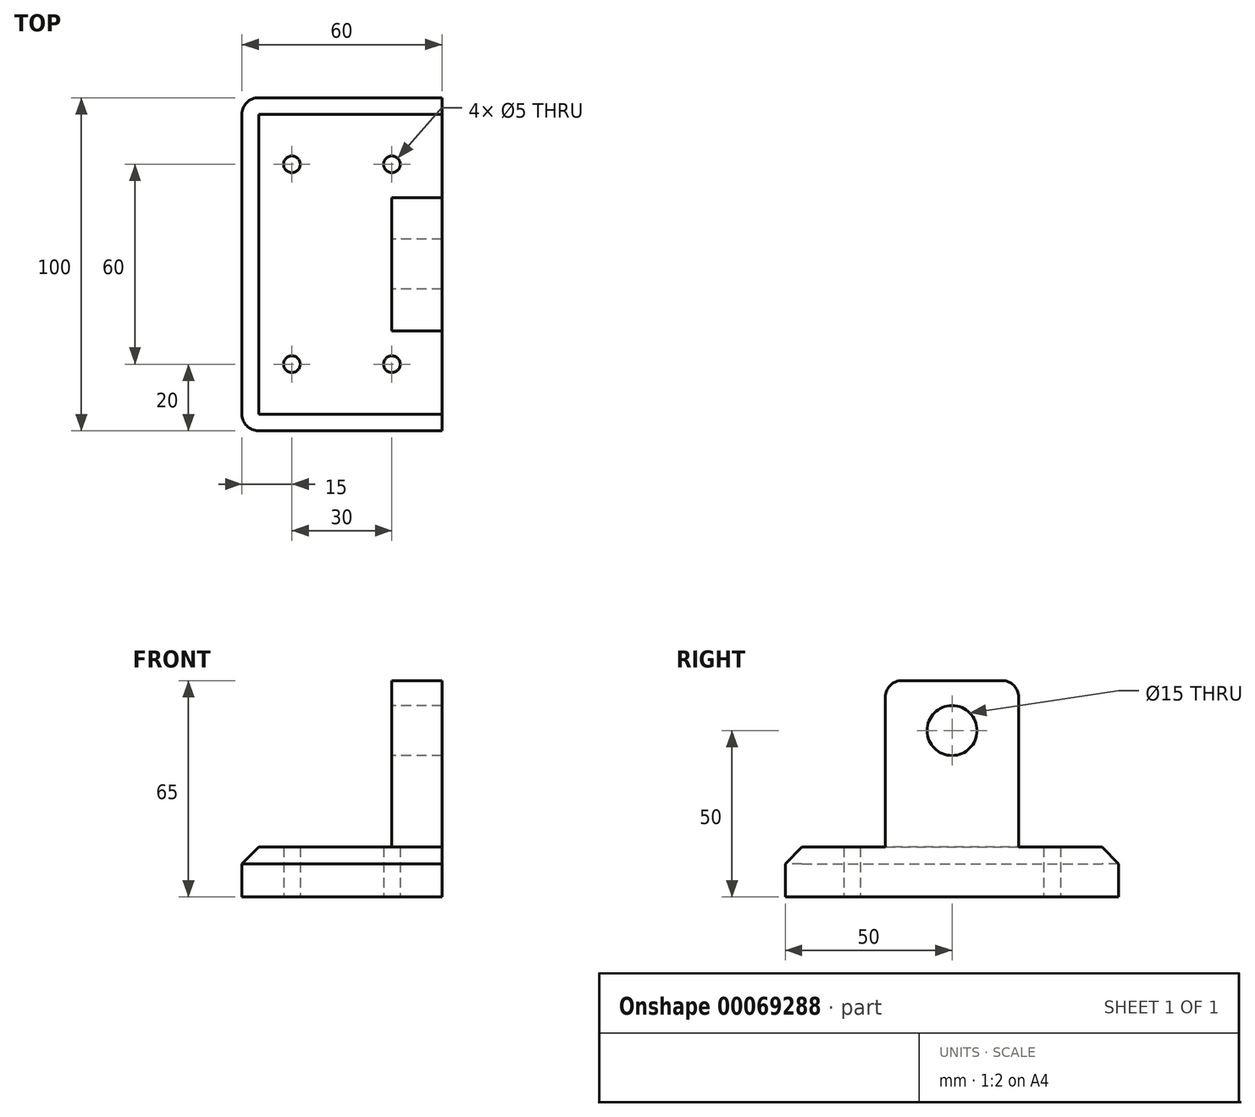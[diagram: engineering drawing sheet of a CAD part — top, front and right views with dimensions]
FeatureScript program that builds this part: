
annotation { "Feature Type Name" : "Feature", "Feature Type Description" : "" }
export const myFeature = defineFeature(function(context is Context, id is Id, definition is map)
    precondition{}
    {
        {
            var Q0;
            Q0=qCreatedBy(makeId("Top.planeOp"),FACE);
            var sketch = newSketch(context, id + "F0", { "sketchPlane" : qUnion([Q0])});
            skLineSegment(sketch, "E0.rect.bottom", {"start": v(30, -50) * mm, "end": v(-25, -50) * mm});
            skLineSegment(sketch, "E0.rect.top", {"start": v(30, 50) * mm, "end": v(-25, 50) * mm});
            skLineSegment(sketch, "E0.rect.left", {"start": v(30, -50) * mm, "end": v(30, 50) * mm});
            skLineSegment(sketch, "E0.rect.right", {"start": v(-30, -45) * mm, "end": v(-30, 45) * mm});
            skPoint(sketch, "E0.rect.middle", {"position": v(0, 0) * mm});
            skPoint(sketch, "E1.visualSharp", {"position": v(-30, 50) * mm});
            skArc(sketch, "E1.filletArc", {"start": v(-25, 50) * mm, "mid": v(-28.54, 48.54) * mm, "end": v(-30, 45) * mm});
            skPoint(sketch, "E2.visualSharp", {"position": v(-30, -50) * mm});
            skArc(sketch, "E2.filletArc", {"start": v(-30, -45) * mm, "mid": v(-28.54, -48.54) * mm, "end": v(-25, -50) * mm});
            skSolve(sketch);
        }
        {
            var Q0;
            Q0=makeQuery(id+"F0.imprint","IMPRINT",FACE,{"disambiguationData":[TD([[makeQuery(id+"F0.imprint","IMPRINT",EDGE,{"derivedFrom":sQuery(id+"F0.wireOp",EDGE,"E0.rect.bottom")}),-1.0]])]});
            extrude(context, id + "F1", {"entities" : qUnion([Q0]), "depth" : 15 * mm});
        }
        {
            var Q0;
            Q0=makeQuery(id+"F1.opExtrude","SWEPT_FACE",FACE,{"disambiguationData":[OSD([sQuery(id+"F0.wireOp",EDGE,"E0.rect.left")])]});
            var sketch = newSketch(context, id + "F2", { "sketchPlane" : qUnion([Q0])});
            skLineSegment(sketch, "E3.bottom", {"start": v(-20, 15) * mm, "end": v(20, 15) * mm});
            skLineSegment(sketch, "E3.top", {"start": v(-20, 65) * mm, "end": v(20, 65) * mm});
            skLineSegment(sketch, "E3.left", {"start": v(-20, 15) * mm, "end": v(-20, 65) * mm});
            skLineSegment(sketch, "E3.right", {"start": v(20, 15) * mm, "end": v(20, 65) * mm});
            skSolve(sketch);
        }
        {
            var Q0;
            Q0 = qSketchRegion(id + "F2", true);
            extrude(context, id + "F3", {"entities" : qUnion([Q0]), "operationType" : NewBodyOperationType.ADD, "oppositeDirection" : true, "depth" : 15 * mm});
        }
        {
            var Q0;
            Q0=makeQuery(id+"F3.opExtrude","SWEPT_EDGE",EDGE,{"disambiguationData":[OSD([sQuery(id+"F0.wireOp",EDGE,"E0.rect.left"),sQuery(id+"F2.wireOp",EDGE,"E3.bottom"),sQuery(id+"F2.wireOp",EDGE,"E3.left")])]});
            var Q1;
            Q1=makeQuery(id+"F3.opExtrude","CAP_EDGE",EDGE,{"disambiguationData":[OSD([sQuery(id+"F2.wireOp",EDGE,"E3.bottom")])],"isStart":false});
            var Q2;
            Q2=makeQuery(id+"F3.opExtrude","SWEPT_EDGE",EDGE,{"disambiguationData":[OSD([sQuery(id+"F0.wireOp",EDGE,"E0.rect.left"),sQuery(id+"F2.wireOp",EDGE,"E3.bottom"),sQuery(id+"F2.wireOp",EDGE,"E3.right")])]});
            var Q3;
            Q3=makeQuery(id+"F3.opExtrude","SWEPT_EDGE",EDGE,{"disambiguationData":[OSD([sQuery(id+"F2.wireOp",EDGE,"E3.top"),sQuery(id+"F2.wireOp",EDGE,"E3.left")])]});
            var Q4;
            Q4=makeQuery(id+"F3.opExtrude","SWEPT_EDGE",EDGE,{"disambiguationData":[OSD([sQuery(id+"F2.wireOp",EDGE,"E3.top"),sQuery(id+"F2.wireOp",EDGE,"E3.right")])]});
            fillet(context, id + "F4", {"entities" : qUnion([Q0, Q1, Q2, Q3, Q4]), "radius" : 5 * mm, "tangentPropagation" : true, "allowEdgeOverflow" : false});
        }
        {
            var Q0;
            Q0=makeQuery(id+"F1.opExtrude","CAP_EDGE",EDGE,{"disambiguationData":[OSD([sQuery(id+"F0.wireOp",EDGE,"E0.rect.top")])],"isStart":false});
            var Q1;
            Q1=makeQuery(id+"F1.opExtrude","CAP_EDGE",EDGE,{"disambiguationData":[OSD([sQuery(id+"F0.wireOp",EDGE,"E1.filletArc")])],"isStart":false});
            var Q2;
            Q2=makeQuery(id+"F1.opExtrude","CAP_EDGE",EDGE,{"disambiguationData":[OSD([sQuery(id+"F0.wireOp",EDGE,"E0.rect.right")])],"isStart":false});
            var Q3;
            Q3=makeQuery(id+"F1.opExtrude","CAP_EDGE",EDGE,{"disambiguationData":[OSD([sQuery(id+"F0.wireOp",EDGE,"E2.filletArc")])],"isStart":false});
            var Q4;
            Q4=makeQuery(id+"F1.opExtrude","CAP_EDGE",EDGE,{"disambiguationData":[OSD([sQuery(id+"F0.wireOp",EDGE,"E0.rect.bottom")])],"isStart":false});
            chamfer(context, id + "F5", {"entities" : qUnion([Q0, Q1, Q2, Q3, Q4]), "width" : 5 * mm, "tangentPropagation" : true});
        }
        {
            var Q0;
            Q0=makeQuery(id+"F3.opExtrude","CAP_FACE",FACE,{"disambiguationData":[OSD([sQuery(id+"F2.wireOp",EDGE,"E3.bottom"),sQuery(id+"F2.wireOp",EDGE,"E3.top"),sQuery(id+"F2.wireOp",EDGE,"E3.left"),sQuery(id+"F2.wireOp",EDGE,"E3.right")])],"isStart":false});
            var sketch = newSketch(context, id + "F6", { "sketchPlane" : qUnion([Q0])});
            skLineSegment(sketch, "E4", {"start": v(0, 65) * mm, "end": v(0, 20) * mm, "construction": true});
            skCircle(sketch, "E5", {"center": v(0, 50) * mm, "radius": 7.5 * mm});
            skSolve(sketch);
        }
        {
            var Q0;
            Q0 = qSketchRegion(id + "F6", true);
            extrude(context, id + "F7", {"entities" : qUnion([Q0]), "operationType" : NewBodyOperationType.REMOVE, "endBound" : BoundingType.UP_TO_NEXT, "oppositeDirection" : true, "depth" : 25 * mm});
        }
        {
            var Q0;
            Q0=makeQuery(id+"F1.opExtrude","CAP_FACE",FACE,{"disambiguationData":[OSD([sQuery(id+"F0.wireOp",EDGE,"E0.rect.bottom"),sQuery(id+"F0.wireOp",EDGE,"E0.rect.top"),sQuery(id+"F0.wireOp",EDGE,"E0.rect.left"),sQuery(id+"F0.wireOp",EDGE,"E0.rect.right"),sQuery(id+"F0.wireOp",EDGE,"E1.filletArc"),sQuery(id+"F0.wireOp",EDGE,"E2.filletArc")])],"isStart":true});
            var sketch = newSketch(context, id + "F8", { "sketchPlane" : qUnion([Q0])});
            skCircle(sketch, "E6", {"center": v(-15, -30) * mm, "radius": 2.5 * mm});
            skCircle(sketch, "E7.0.1.0", {"center": v(-15, 30) * mm, "radius": 2.5 * mm});
            skCircle(sketch, "E7.1.0.0", {"center": v(15, -30) * mm, "radius": 2.5 * mm});
            skCircle(sketch, "E7.1.1.0", {"center": v(15, 30) * mm, "radius": 2.5 * mm});
            skLineSegment(sketch, "E7.direction1", {"start": v(-15, -30) * mm, "end": v(15, -30) * mm, "construction": true});
            skLineSegment(sketch, "E7.direction2", {"start": v(-15, -30) * mm, "end": v(-15, 30) * mm, "construction": true});
            skSolve(sketch);
        }
        {
            var Q0;
            Q0 = qSketchRegion(id + "F8", true);
            extrude(context, id + "F9", {"entities" : qUnion([Q0]), "operationType" : NewBodyOperationType.REMOVE, "endBound" : BoundingType.UP_TO_NEXT, "oppositeDirection" : true, "depth" : 25 * mm});
        }
    });
